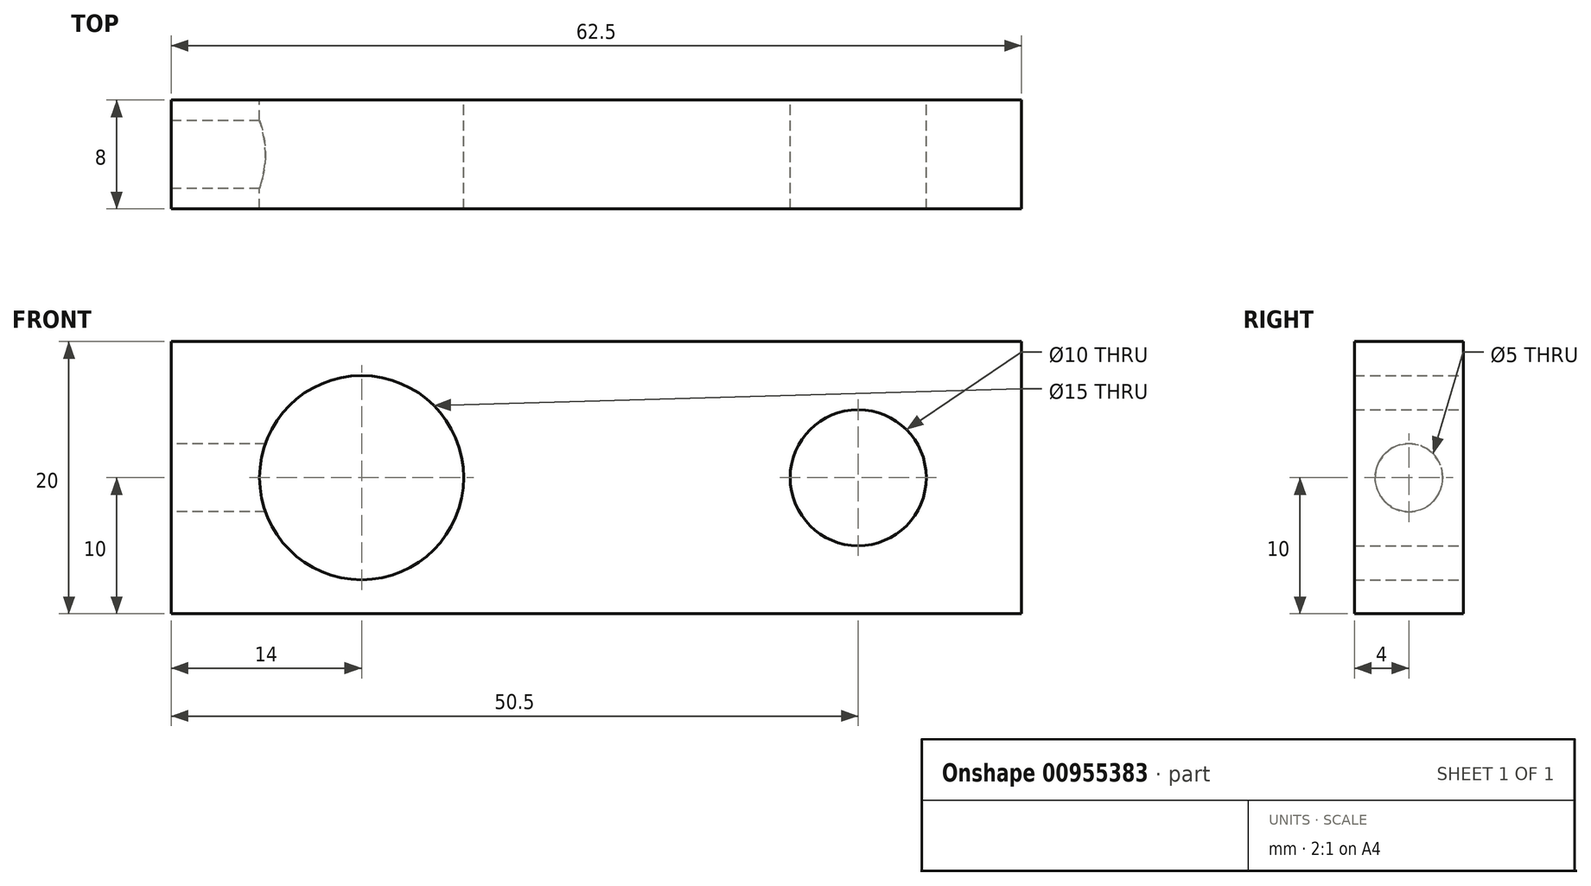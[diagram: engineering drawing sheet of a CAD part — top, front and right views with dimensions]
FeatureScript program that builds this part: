
annotation { "Feature Type Name" : "Feature", "Feature Type Description" : "" }
export const myFeature = defineFeature(function(context is Context, id is Id, definition is map)
    precondition{}
    {
        {
            var Q0;
            Q0=qCreatedBy(makeId("Front.planeOp"),FACE);
            var sketch = newSketch(context, id + "F0", { "sketchPlane" : qUnion([Q0])});
            skLineSegment(sketch, "E0.bottom", {"start": v(29.25, 10) * mm, "end": v(-33.25, 10) * mm});
            skLineSegment(sketch, "E0.top", {"start": v(29.25, -10) * mm, "end": v(-33.25, -10) * mm});
            skLineSegment(sketch, "E0.left", {"start": v(29.25, 10) * mm, "end": v(29.25, -10) * mm});
            skLineSegment(sketch, "E0.right", {"start": v(-33.25, 10) * mm, "end": v(-33.25, -10) * mm});
            skCircle(sketch, "E1", {"center": v(17.25, 0) * mm, "radius": 5 * mm});
            skCircle(sketch, "E2", {"center": v(-19.25, 0) * mm, "radius": 7.5 * mm});
            skSolve(sketch);
        }
        {
            var Q0;
            Q0=makeQuery(id+"F0.imprint","IMPRINT",FACE,{"disambiguationData":[TD([[makeQuery(id+"F0.imprint","IMPRINT",EDGE,{"derivedFrom":sQuery(id+"F0.wireOp",EDGE,"E0.bottom")}),1.0]])]});
            extrude(context, id + "F1", {"entities" : qUnion([Q0]), "depth" : 5.5 * mm, "offsetDistance" : 25 * mm});
        }
        {
            var Q0;
            Q0=makeQuery(id+"F1.opExtrude","CAP_FACE",FACE,{"disambiguationData":[OSD([sQuery(id+"F0.wireOp",EDGE,"E0.bottom"),sQuery(id+"F0.wireOp",EDGE,"E0.top"),sQuery(id+"F0.wireOp",EDGE,"E0.left"),sQuery(id+"F0.wireOp",EDGE,"E0.right"),sQuery(id+"F0.wireOp",EDGE,"E1")])],"isStart":false});
            extrude(context, id + "F2", {"entities" : qUnion([Q0]), "operationType" : NewBodyOperationType.ADD, "depth" : 2.5 * mm, "offsetDistance" : 25 * mm});
        }
        {
            var Q0;
            {var subQ0=sQuery(id+"F0.wireOp",EDGE,"E0.right");Q0=makeQuery(id+"F2.boolean.opBoolean","MERGE",FACE,{"derivedFrom":[makeQuery(id+"F1.opExtrude","SWEPT_FACE",FACE,{"disambiguationData":[OSD([subQ0])]}),makeQuery(id+"F2.opExtrude","SWEPT_FACE",FACE,{"disambiguationData":[OSD([subQ0])]})]});}
            var sketch = newSketch(context, id + "F3", { "sketchPlane" : qUnion([Q0])});
            skCircle(sketch, "E3", {"center": v(4, 0) * mm, "radius": 2.5 * mm});
            skSolve(sketch);
        }
        {
            var Q0;
            Q0=makeQuery(id+"F3.imprint","IMPRINT",FACE,{"disambiguationData":[TD([[makeQuery(id+"F3.imprint","IMPRINT",EDGE,{"derivedFrom":sQuery(id+"F3.wireOp",EDGE,"E3")}),1.0]])]});
            var Q1;
            Q1=makeQuery(id+"F3.imprint","IMPRINT",FACE,{"disambiguationData":[TD([[makeQuery(id+"F3.imprint","IMPRINT",EDGE,{"derivedFrom":sQuery(id+"F3.wireOp",EDGE,"dEBBMaty-YIWb-ton4-p6e1-xG2H2Vy74N7O")}),1.0]])]});
            extrude(context, id + "F4", {"entities" : qUnion([Q0, Q1]), "operationType" : NewBodyOperationType.REMOVE, "oppositeDirection" : true, "depth" : 10 * mm, "offsetDistance" : 25 * mm});
        }
    });
